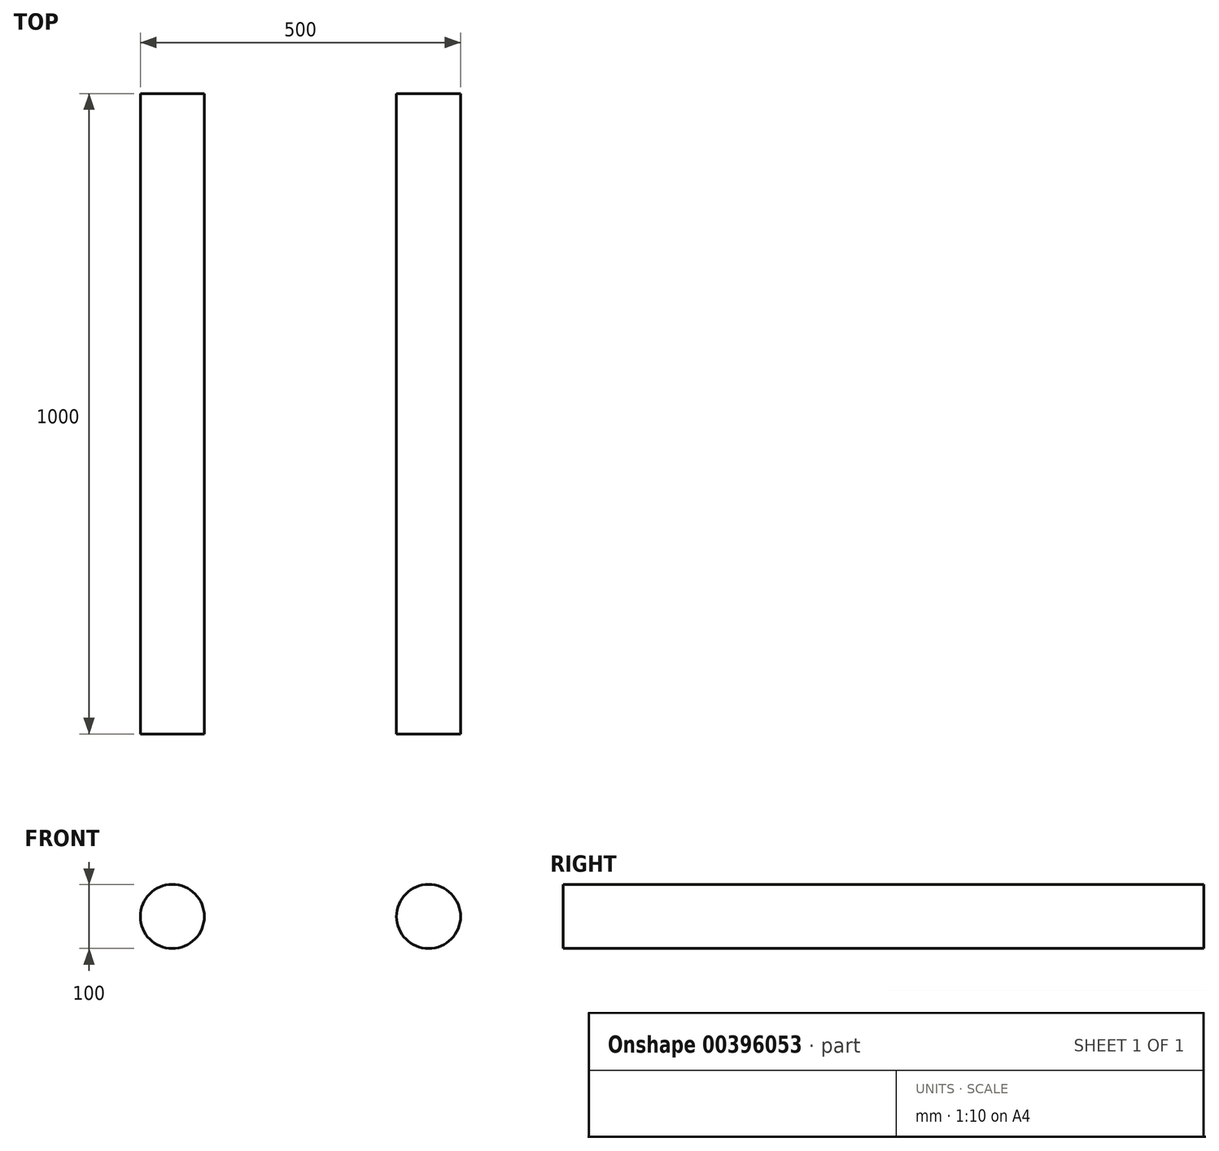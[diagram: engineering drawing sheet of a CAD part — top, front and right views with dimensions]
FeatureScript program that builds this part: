
annotation { "Feature Type Name" : "Feature", "Feature Type Description" : "" }
export const myFeature = defineFeature(function(context is Context, id is Id, definition is map)
    precondition{}
    {
        {
            var Q0;
            Q0=qCreatedBy(makeId("Front.planeOp"),FACE);
            var sketch = newSketch(context, id + "F0", { "sketchPlane" : qUnion([Q0])});
            skCircle(sketch, "E0", {"center": v(-200, 0) * mm, "radius": 50 * mm});
            skCircle(sketch, "E1", {"center": v(200, 0) * mm, "radius": 50 * mm});
            skSolve(sketch);
        }
        {
            var Q0;
            Q0 = qSketchRegion(id + "F0", true);
            extrude(context, id + "F1", {"entities" : qUnion([Q0]), "depth" : 1000 * mm});
        }
    });
